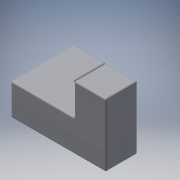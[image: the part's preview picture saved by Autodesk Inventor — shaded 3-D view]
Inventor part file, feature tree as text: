
AUTODESK INVENTOR PART (.ipt)
format: ipt  version: 2016 (Build 200138000, 138)  size: 155,136 bytes
history: native  units: in
note: dims shown in document units (in); Inventor stores cm internally (conversion verified against a paired STEP export)
features: plane x8, extrude x2, other x1, fillet x1, sketch x1
ambient origin geometry x8: Origin, YZ Plane, XZ Plane, XY Plane, X Axis, Y Axis, Z Axis, Center Point
bodies: Solid1 (feature_tree)
feature tree (13):
  other  "Cube Master.ipt"
  extrude  "Extrusion1"  Depth=0.3937in
  extrude  "Extrusion2"  Depth=0.0193in TaperAngle=0.0deg
  fillet  "Fillet1"  Radius=1.0in
  sketch  "Sketch1"  dims[d0=0.3937in d1=0.3937in d2=1.0in d3=0.0in d4=1.0in d5=0.0in d7=0.0193in d8=0.0193in]
  plane  "Work Plane1"
  plane  "Work Plane2"
  plane  "Work Plane3"
  plane  "Work Plane4"
  plane  "Work Plane5"
  plane  "Work Plane6"
  plane  "Work Plane7"
  plane  "Work Plane8"
